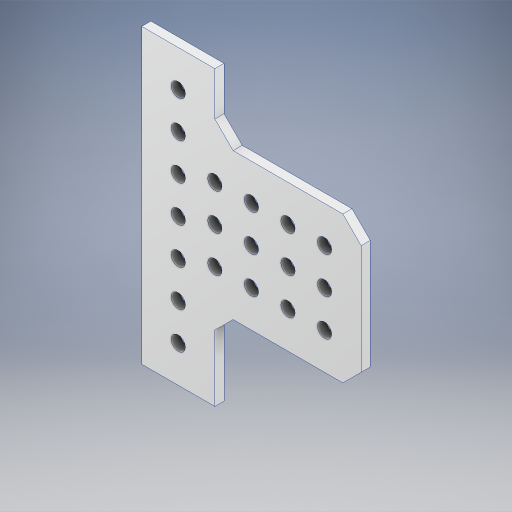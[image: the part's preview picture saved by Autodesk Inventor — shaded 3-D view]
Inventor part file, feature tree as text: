
AUTODESK INVENTOR PART (.ipt)
format: ipt  version: 2024.2 (Build 282272000, 272)  size: 343,552 bytes
history: native  units: in
note: dims shown in document units (in); Inventor stores cm internally (conversion verified against a paired STEP export)
features: extrude x1, sketch x1
ambient origin geometry x8: Origin, YZ Plane, XZ Plane, XY Plane, X Axis, Y Axis, Z Axis, Center Point
bodies: Body1 (feature_tree)
feature tree (2):
  extrude  "Extrusion2"  Depth=0.5in
  sketch  "Sketch1"  dims[d0=0.196in d1=0.196in d2=0.346in d3=0.5in d4=1.5748in d6=0.5in d7=0.3937in d9=1.0in d11=1.5748in d13=0.5in d14=0.3937in d16=1.0in d26=1.1811in d28=0.5in d29=0.3937in d31=1.0in d33=1.1811in d35=0.5in d36=0.3937in d38=1.0in d42=0.5in d43=0.5in d44=2.0in d45=0.654in d46=1.0in d47=3.5in d48=0.25in d49=0.25in d50=0.25in d51=0.25in d52=0.25in d53=0.25in d54=0.25in d55=0.25in d56=0.125in d57=0.0in d58=0.7874in d60=0.5in d61=0.3937in d63=1.0in d66=0.5in]
